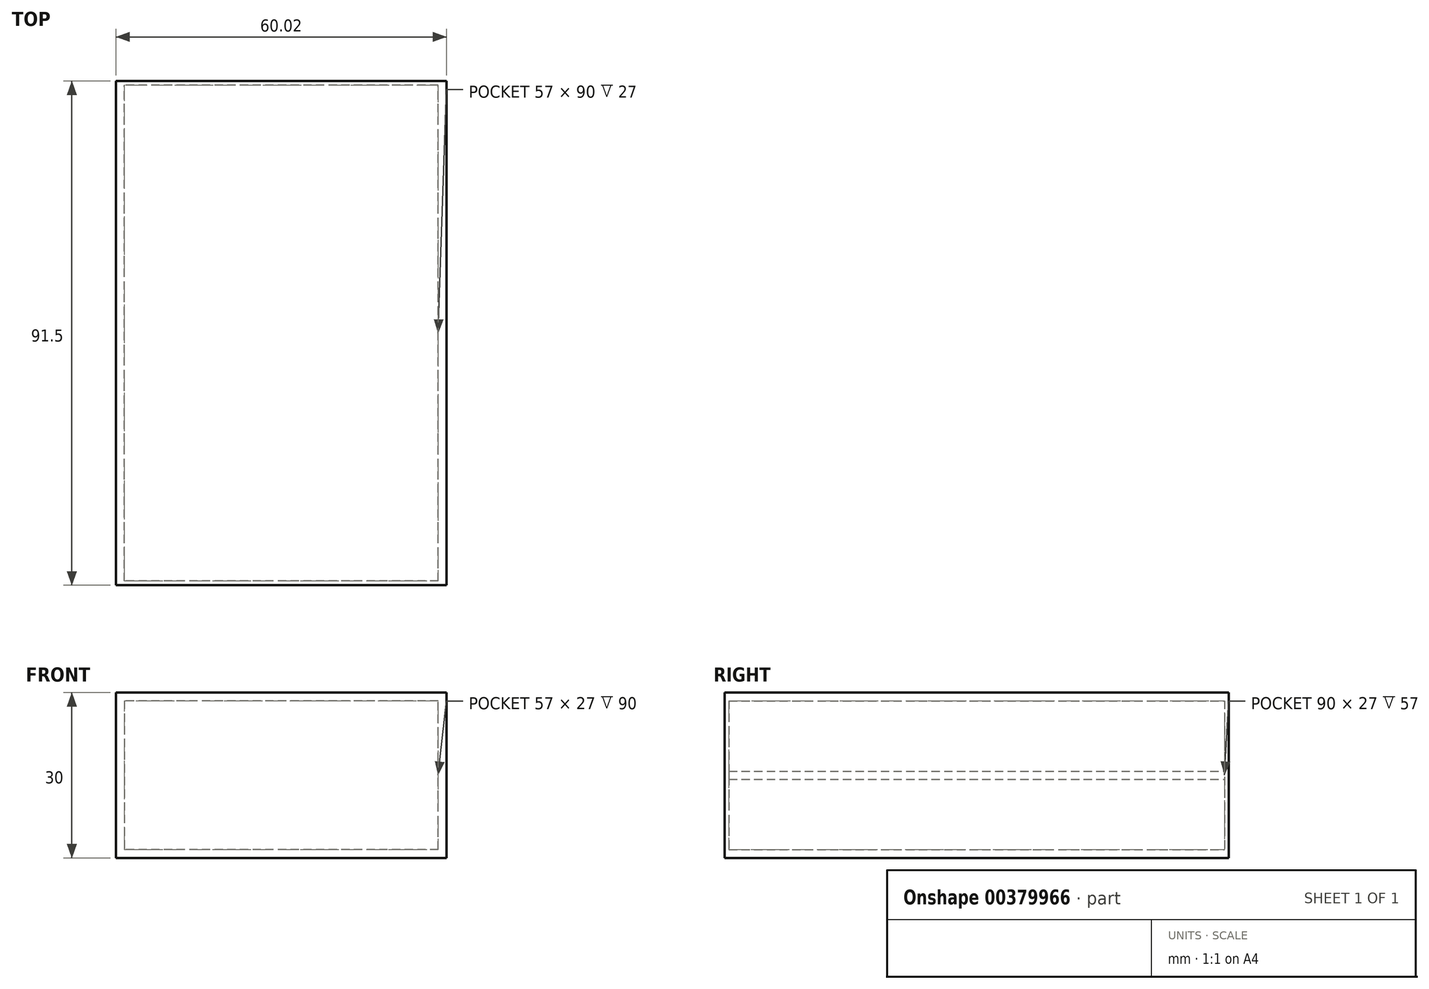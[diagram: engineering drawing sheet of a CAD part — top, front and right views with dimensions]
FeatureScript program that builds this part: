
annotation { "Feature Type Name" : "Feature", "Feature Type Description" : "" }
export const myFeature = defineFeature(function(context is Context, id is Id, definition is map)
    precondition{}
    {
        {
            var Q0;
            Q0=qCreatedBy(makeId("Front.planeOp"),FACE);
            var sketch = newSketch(context, id + "F0", { "sketchPlane" : qUnion([Q0])});
            skLineSegment(sketch, "E0", {"start": v(-22.72, 0) * mm, "end": v(-22.72, 15) * mm});
            skLineSegment(sketch, "E1", {"start": v(-22.72, 15) * mm, "end": v(37.28, 15) * mm});
            skLineSegment(sketch, "E2", {"start": v(37.28, 15) * mm, "end": v(37.28, 0) * mm});
            skLineSegment(sketch, "E3", {"start": v(35.78, 0) * mm, "end": v(35.78, 13.5) * mm});
            skLineSegment(sketch, "E4", {"start": v(35.78, 13.5) * mm, "end": v(-21.22, 13.5) * mm});
            skLineSegment(sketch, "E5", {"start": v(-21.22, 13.5) * mm, "end": v(-21.22, 0) * mm});
            skLineSegment(sketch, "E6", {"start": v(-22.72, 0) * mm, "end": v(-22.72, -0.75) * mm});
            skLineSegment(sketch, "E7", {"start": v(-22.72, -0.75) * mm, "end": v(-21.97, -0.75) * mm});
            skLineSegment(sketch, "E8", {"start": v(-21.97, -0.75) * mm, "end": v(-21.97, 0) * mm});
            skLineSegment(sketch, "E9", {"start": v(37.28, 0) * mm, "end": v(37.28, -0.75) * mm});
            skLineSegment(sketch, "E10", {"start": v(37.28, -0.75) * mm, "end": v(36.53, -0.75) * mm});
            skLineSegment(sketch, "E11", {"start": v(36.53, -0.75) * mm, "end": v(36.53, 0) * mm});
            skLineSegment(sketch, "E12", {"start": v(35.78, 0) * mm, "end": v(36.53, 0) * mm});
            skLineSegment(sketch, "E13", {"start": v(-21.97, 0) * mm, "end": v(-21.22, 0) * mm});
            skSolve(sketch);
        }
        {
            var Q0;
            Q0=makeQuery(id+"F0.imprint","IMPRINT",FACE,{"disambiguationData":[TD([[makeQuery(id+"F0.imprint","IMPRINT",EDGE,{"derivedFrom":sQuery(id+"F0.wireOp",EDGE,"E0")}),-1.0]])]});
            extrude(context, id + "F1", {"entities" : qUnion([Q0]), "depth" : 90 * mm});
        }
        {
            var Q0;
            Q0=qCreatedBy(makeId("Front.planeOp"),FACE);
            var sketch = newSketch(context, id + "F2", { "sketchPlane" : qUnion([Q0])});
            skLineSegment(sketch, "E14.bottom", {"start": v(37.29, 15) * mm, "end": v(-22.71, 15) * mm});
            skLineSegment(sketch, "E14.top", {"start": v(37.29, 0) * mm, "end": v(-22.71, 0) * mm});
            skLineSegment(sketch, "E14.left", {"start": v(37.29, 15) * mm, "end": v(37.29, 0) * mm});
            skLineSegment(sketch, "E14.right", {"start": v(-22.71, 15) * mm, "end": v(-22.71, 0) * mm});
            skSolve(sketch);
        }
        {
            var Q0;
            Q0=makeQuery(id+"F2.imprint","IMPRINT",FACE,{"disambiguationData":[TD([[makeQuery(id+"F2.imprint","IMPRINT",EDGE,{"derivedFrom":sQuery(id+"F2.wireOp",EDGE,"E14.bottom")}),1.0]])]});
            extrude(context, id + "F3", {"entities" : qUnion([Q0]), "operationType" : NewBodyOperationType.ADD, "oppositeDirection" : true, "depth" : .75 * mm});
        }
        {
            var Q0;
            Q0=makeQuery(id+"F1.opExtrude","CAP_FACE",FACE,{"disambiguationData":[OSD([sQuery(id+"F0.wireOp",EDGE,"E0"),sQuery(id+"F0.wireOp",EDGE,"E1"),sQuery(id+"F0.wireOp",EDGE,"E2"),sQuery(id+"F0.wireOp",EDGE,"E3"),sQuery(id+"F0.wireOp",EDGE,"E4"),sQuery(id+"F0.wireOp",EDGE,"E5"),sQuery(id+"F0.wireOp",EDGE,"E6"),sQuery(id+"F0.wireOp",EDGE,"E7"),sQuery(id+"F0.wireOp",EDGE,"E8"),sQuery(id+"F0.wireOp",EDGE,"E9"),sQuery(id+"F0.wireOp",EDGE,"E10"),sQuery(id+"F0.wireOp",EDGE,"E11"),sQuery(id+"F0.wireOp",EDGE,"E12"),sQuery(id+"F0.wireOp",EDGE,"E13")])],"isStart":false});
            var sketch = newSketch(context, id + "F4", { "sketchPlane" : qUnion([Q0])});
            skLineSegment(sketch, "E15.bottom", {"start": v(-22.72, 15) * mm, "end": v(37.28, 15) * mm});
            skLineSegment(sketch, "E15.top", {"start": v(-22.72, 0) * mm, "end": v(37.28, 0) * mm});
            skLineSegment(sketch, "E15.left", {"start": v(-22.72, 15) * mm, "end": v(-22.72, 0) * mm});
            skLineSegment(sketch, "E15.right", {"start": v(37.28, 15) * mm, "end": v(37.28, 0) * mm});
            skSolve(sketch);
        }
        {
            var Q0;
            Q0 = qSketchRegion(id + "F4", true);
            extrude(context, id + "F5", {"entities" : qUnion([Q0]), "operationType" : NewBodyOperationType.ADD, "depth" : .75 * mm});
        }
        {
            var Q0;
            Q0=makeQuery(id+"F1.opExtrude","SWEPT_BODY",BODY,{"disambiguationData":[OSD([sQuery(id+"F0.wireOp",EDGE,"E0"),sQuery(id+"F0.wireOp",EDGE,"E1"),sQuery(id+"F0.wireOp",EDGE,"E2"),sQuery(id+"F0.wireOp",EDGE,"E3"),sQuery(id+"F0.wireOp",EDGE,"E4"),sQuery(id+"F0.wireOp",EDGE,"E5"),sQuery(id+"F0.wireOp",EDGE,"E6"),sQuery(id+"F0.wireOp",EDGE,"E7"),sQuery(id+"F0.wireOp",EDGE,"E8"),sQuery(id+"F0.wireOp",EDGE,"E9"),sQuery(id+"F0.wireOp",EDGE,"E10"),sQuery(id+"F0.wireOp",EDGE,"E11"),sQuery(id+"F0.wireOp",EDGE,"E12"),sQuery(id+"F0.wireOp",EDGE,"E13")])]});
            var Q1;
            Q1=qCreatedBy(makeId("Top.planeOp"),FACE);
            mirror(context, id + "F6", {"entities" : qUnion([Q0]), "mirrorPlane" : qUnion([Q1])});
        }
        {
            var Q0;
            Q0=qCreatedBy(makeId("Front.planeOp"),FACE);
            var sketch = newSketch(context, id + "F7", { "sketchPlane" : qUnion([Q0])});
            skLineSegment(sketch, "E16.bottom", {"start": v(-22.73, 0.76) * mm, "end": v(-21.97, 0.76) * mm});
            skLineSegment(sketch, "E16.top", {"start": v(-22.73, -0.76) * mm, "end": v(-21.97, -0.76) * mm});
            skLineSegment(sketch, "E16.left", {"start": v(-22.73, 0.76) * mm, "end": v(-22.73, -0.76) * mm});
            skLineSegment(sketch, "E16.right", {"start": v(-21.97, 0.76) * mm, "end": v(-21.97, -0.76) * mm});
            skSolve(sketch);
        }
        {
            var Q0;
            Q0 = qSketchRegion(id + "F7", true);
            extrude(context, id + "F8", {"entities" : qUnion([Q0]), "operationType" : NewBodyOperationType.ADD, "depth" : 90 * mm});
        }
    });
